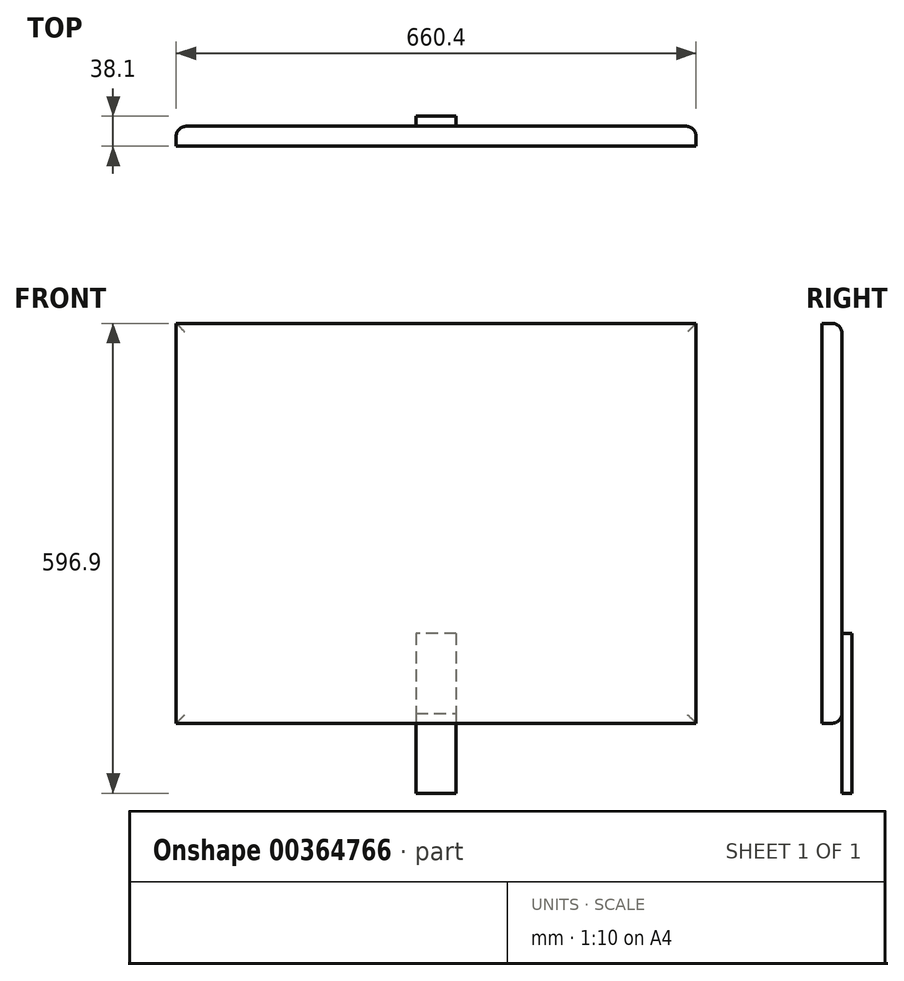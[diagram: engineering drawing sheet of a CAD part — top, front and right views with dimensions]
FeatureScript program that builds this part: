
annotation { "Feature Type Name" : "Feature", "Feature Type Description" : "" }
export const myFeature = defineFeature(function(context is Context, id is Id, definition is map)
    precondition{}
    {
        {
            var Q0;
            Q0=qCreatedBy(makeId("Front.planeOp"),FACE);
            var sketch = newSketch(context, id + "F0", { "sketchPlane" : qUnion([Q0])});
            skLineSegment(sketch, "E0.bottom", {"start": v(0, 0) * mm, "end": v(660.4, 0) * mm});
            skLineSegment(sketch, "E0.top", {"start": v(0, 508) * mm, "end": v(660.4, 508) * mm});
            skLineSegment(sketch, "E0.left", {"start": v(0, 0) * mm, "end": v(0, 508) * mm});
            skLineSegment(sketch, "E0.right", {"start": v(660.4, 0) * mm, "end": v(660.4, 508) * mm});
            skSolve(sketch);
        }
        {
            var Q0;
            Q0 = qSketchRegion(id + "F0", true);
            extrude(context, id + "F1", {"entities" : qUnion([Q0]), "depth" : 25.4 * mm});
        }
        {
            var Q0;
            Q0=makeQuery(id+"F1.opExtrude","CAP_EDGE",EDGE,{"disambiguationData":[OSD([sQuery(id+"F0.wireOp",EDGE,"E0.top")])],"isStart":true});
            var Q1;
            Q1=makeQuery(id+"F1.opExtrude","CAP_EDGE",EDGE,{"disambiguationData":[OSD([sQuery(id+"F0.wireOp",EDGE,"E0.right")])],"isStart":true});
            var Q2;
            Q2=makeQuery(id+"F1.opExtrude","CAP_EDGE",EDGE,{"disambiguationData":[OSD([sQuery(id+"F0.wireOp",EDGE,"E0.bottom")])],"isStart":true});
            var Q3;
            Q3=makeQuery(id+"F1.opExtrude","CAP_EDGE",EDGE,{"disambiguationData":[OSD([sQuery(id+"F0.wireOp",EDGE,"E0.left")])],"isStart":true});
            fillet(context, id + "F2", {"entities" : qUnion([Q0, Q1, Q2, Q3]), "radius" : 12.7 * mm, "tangentPropagation" : true, "allowEdgeOverflow" : false});
        }
        {
            var Q0;
            Q0=makeQuery(id+"F1.opExtrude","CAP_FACE",FACE,{"disambiguationData":[OSD([sQuery(id+"F0.wireOp",EDGE,"E0.bottom"),sQuery(id+"F0.wireOp",EDGE,"E0.top"),sQuery(id+"F0.wireOp",EDGE,"E0.left"),sQuery(id+"F0.wireOp",EDGE,"E0.right")])],"isStart":true});
            var sketch = newSketch(context, id + "F3", { "sketchPlane" : qUnion([Q0])});
            skLineSegment(sketch, "E1.bottom", {"start": v(-355.6, 114.3) * mm, "end": v(-304.8, 114.3) * mm});
            skLineSegment(sketch, "E1.top", {"start": v(-355.6, -88.9) * mm, "end": v(-304.8, -88.9) * mm});
            skLineSegment(sketch, "E1.left", {"start": v(-355.6, 114.3) * mm, "end": v(-355.6, -88.9) * mm});
            skLineSegment(sketch, "E1.right", {"start": v(-304.8, 114.3) * mm, "end": v(-304.8, -88.9) * mm});
            skPoint(sketch, "E2", {"position": v(-304.8, 12.7) * mm});
            skPoint(sketch, "E3", {"position": v(-330.2, 12.7) * mm});
            skPoint(sketch, "E4", {"position": v(-330.2, 114.3) * mm});
            skSolve(sketch);
        }
        {
            var Q0;
            Q0 = qSketchRegion(id + "F3", true);
            extrude(context, id + "F4", {"entities" : qUnion([Q0]), "operationType" : NewBodyOperationType.ADD, "depth" : 12.7 * mm});
        }
    });
